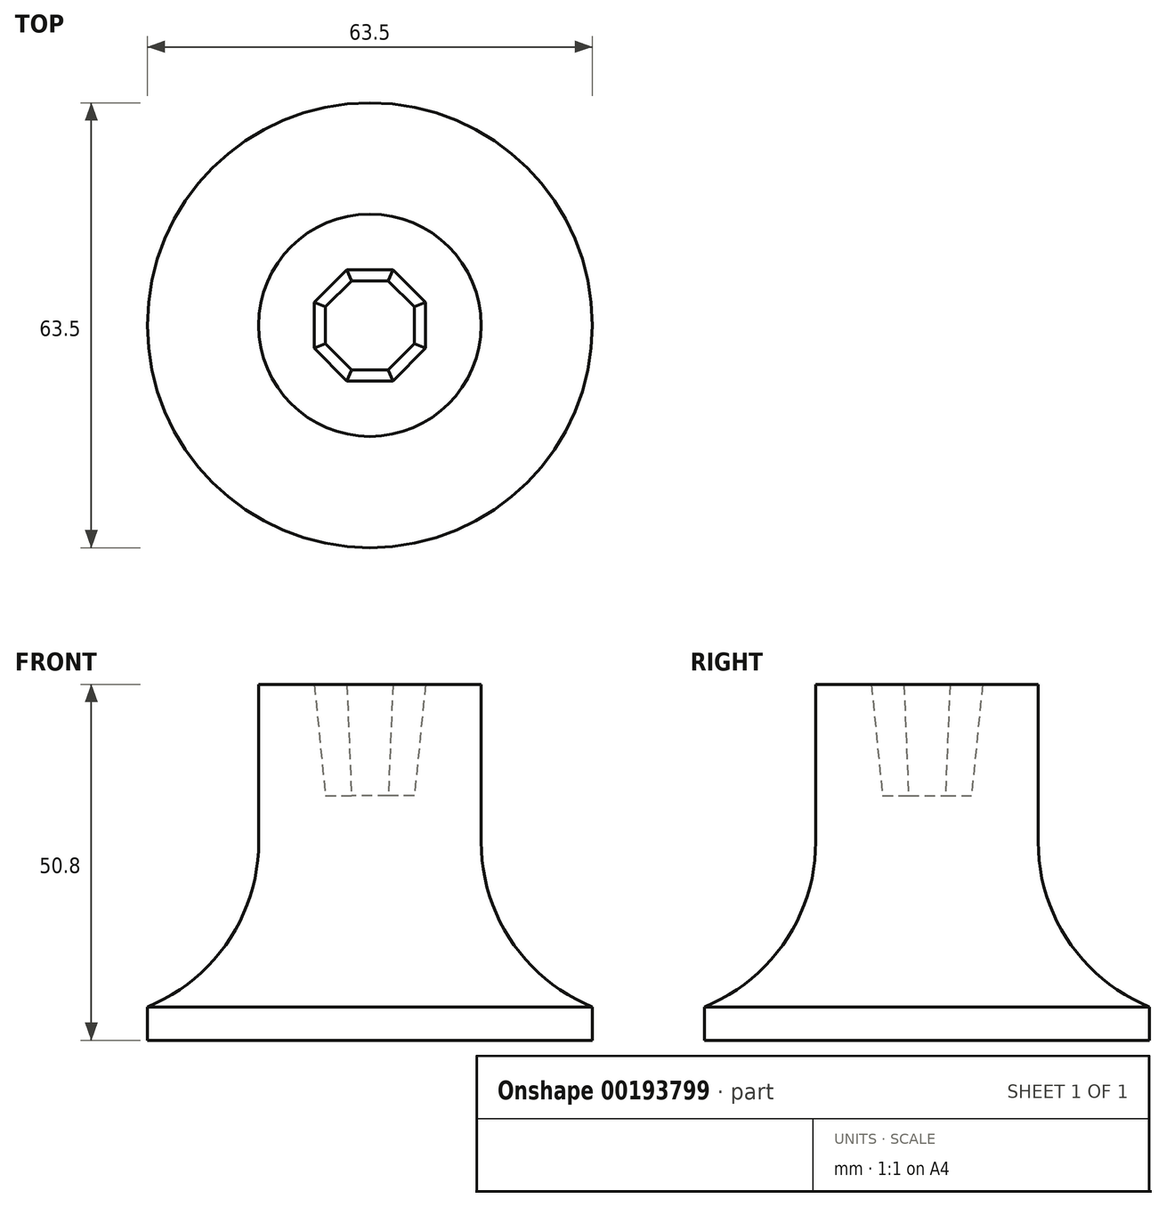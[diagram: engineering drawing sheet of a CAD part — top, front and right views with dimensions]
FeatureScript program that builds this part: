
annotation { "Feature Type Name" : "Feature", "Feature Type Description" : "" }
export const myFeature = defineFeature(function(context is Context, id is Id, definition is map)
    precondition{}
    {
        {
            var Q0;
            Q0=qCreatedBy(makeId("Front.planeOp"),FACE);
            var sketch = newSketch(context, id + "F0", { "sketchPlane" : qUnion([Q0])});
            skLineSegment(sketch, "E0", {"start": v(0, 0) * mm, "end": v(31.75, 0) * mm});
            skLineSegment(sketch, "E1", {"start": v(31.75, 0) * mm, "end": v(31.75, 4.76) * mm});
            skArc(sketch, "E2", {"start": v(15.87, 28.3) * mm, "mid": v(20.21, 14.1) * mm, "end": v(31.75, 4.76) * mm});
            skLineSegment(sketch, "E3", {"start": v(0, 50.8) * mm, "end": v(0, 0) * mm});
            skLineSegment(sketch, "E4", {"start": v(15.87, 28.3) * mm, "end": v(15.87, 50.8) * mm});
            skLineSegment(sketch, "E5", {"start": v(15.87, 50.8) * mm, "end": v(0, 50.8) * mm});
            skSolve(sketch);
        }
        {
            var Q0;
            Q0=makeQuery(id+"F0.imprint","IMPRINT",FACE,{"disambiguationData":[TD([[makeQuery(id+"F0.imprint","IMPRINT",EDGE,{"derivedFrom":sQuery(id+"F0.wireOp",EDGE,"E0")}),1.0]])]});
            var Q1;
            Q1=sQuery(id+"F0.wireOp",EDGE,"E3");
            revolve(context, id + "F1", {"entities" : qUnion([Q0]), "axis" : qUnion([Q1]), "revolveType" : RevolveType.FULL});
        }
        {
            var Q0;
            Q0=makeQuery(id+"F1.opRevolve","SWEPT_FACE",FACE,{"disambiguationData":[OSD([sQuery(id+"F0.wireOp",EDGE,"E5")])]});
            var sketch = newSketch(context, id + "F2", { "sketchPlane" : qUnion([Q0])});
            skLineSegment(sketch, "E6", {"start": v(-3.29, 7.94) * mm, "end": v(3.29, 7.94) * mm});
            skLineSegment(sketch, "E7", {"start": v(3.29, 7.94) * mm, "end": v(7.94, 3.29) * mm});
            skLineSegment(sketch, "E8", {"start": v(7.94, 3.29) * mm, "end": v(7.94, -3.29) * mm});
            skLineSegment(sketch, "E9", {"start": v(7.94, -3.29) * mm, "end": v(3.29, -7.94) * mm});
            skLineSegment(sketch, "E10", {"start": v(3.29, -7.94) * mm, "end": v(-3.29, -7.94) * mm});
            skLineSegment(sketch, "E11", {"start": v(-3.29, -7.94) * mm, "end": v(-7.94, -3.29) * mm});
            skLineSegment(sketch, "E12", {"start": v(-7.94, -3.29) * mm, "end": v(-7.94, 3.29) * mm});
            skLineSegment(sketch, "E13", {"start": v(-7.94, 3.29) * mm, "end": v(-3.29, 7.94) * mm});
            skSolve(sketch);
        }
        {
            var Q0;
            Q0=makeQuery(id+"F2.imprint","IMPRINT",FACE,{"disambiguationData":[TD([[makeQuery(id+"F2.imprint","IMPRINT",EDGE,{"derivedFrom":sQuery(id+"F2.wireOp",EDGE,"E6")}),1.0]])]});
            cPlane(context, id + "F3", {"entities" : qUnion([Q0]), "cplaneType" : CPlaneType.OFFSET, "offset" : 15.88 * mm, "oppositeDirection" : true, "width" : 152.4 * mm, "height" : 152.4 * mm});
        }
        {
            var Q0;
            Q0=qCreatedBy(id+"F3.planeOp",FACE);
            var sketch = newSketch(context, id + "F4", { "sketchPlane" : qUnion([Q0])});
            skLineSegment(sketch, "E14", {"start": v(-2.63, 6.35) * mm, "end": v(2.63, 6.35) * mm});
            skLineSegment(sketch, "E15", {"start": v(2.63, 6.35) * mm, "end": v(6.35, 2.63) * mm});
            skLineSegment(sketch, "E16", {"start": v(6.35, 2.63) * mm, "end": v(6.35, -2.63) * mm});
            skLineSegment(sketch, "E17", {"start": v(6.35, -2.63) * mm, "end": v(2.63, -6.35) * mm});
            skLineSegment(sketch, "E18", {"start": v(2.63, -6.35) * mm, "end": v(-2.63, -6.35) * mm});
            skLineSegment(sketch, "E19", {"start": v(-2.63, -6.35) * mm, "end": v(-6.35, -2.63) * mm});
            skLineSegment(sketch, "E20", {"start": v(-6.35, -2.63) * mm, "end": v(-6.35, 2.63) * mm});
            skLineSegment(sketch, "E21", {"start": v(-6.35, 2.63) * mm, "end": v(-2.63, 6.35) * mm});
            skSolve(sketch);
        }
        {
            var Q1;
            Q1 = qSketchRegion(id + "F2", true);
            var Q2;
            Q2 = qSketchRegion(id + "F4", true);
            loft(context, id + "F5", {"operationType" : NewBodyOperationType.REMOVE, "sheetProfilesArray" : [{ "sheetProfileEntities" : qUnion([Q1]) }, { "sheetProfileEntities" : qUnion([Q2]) }]});
        }
    });
